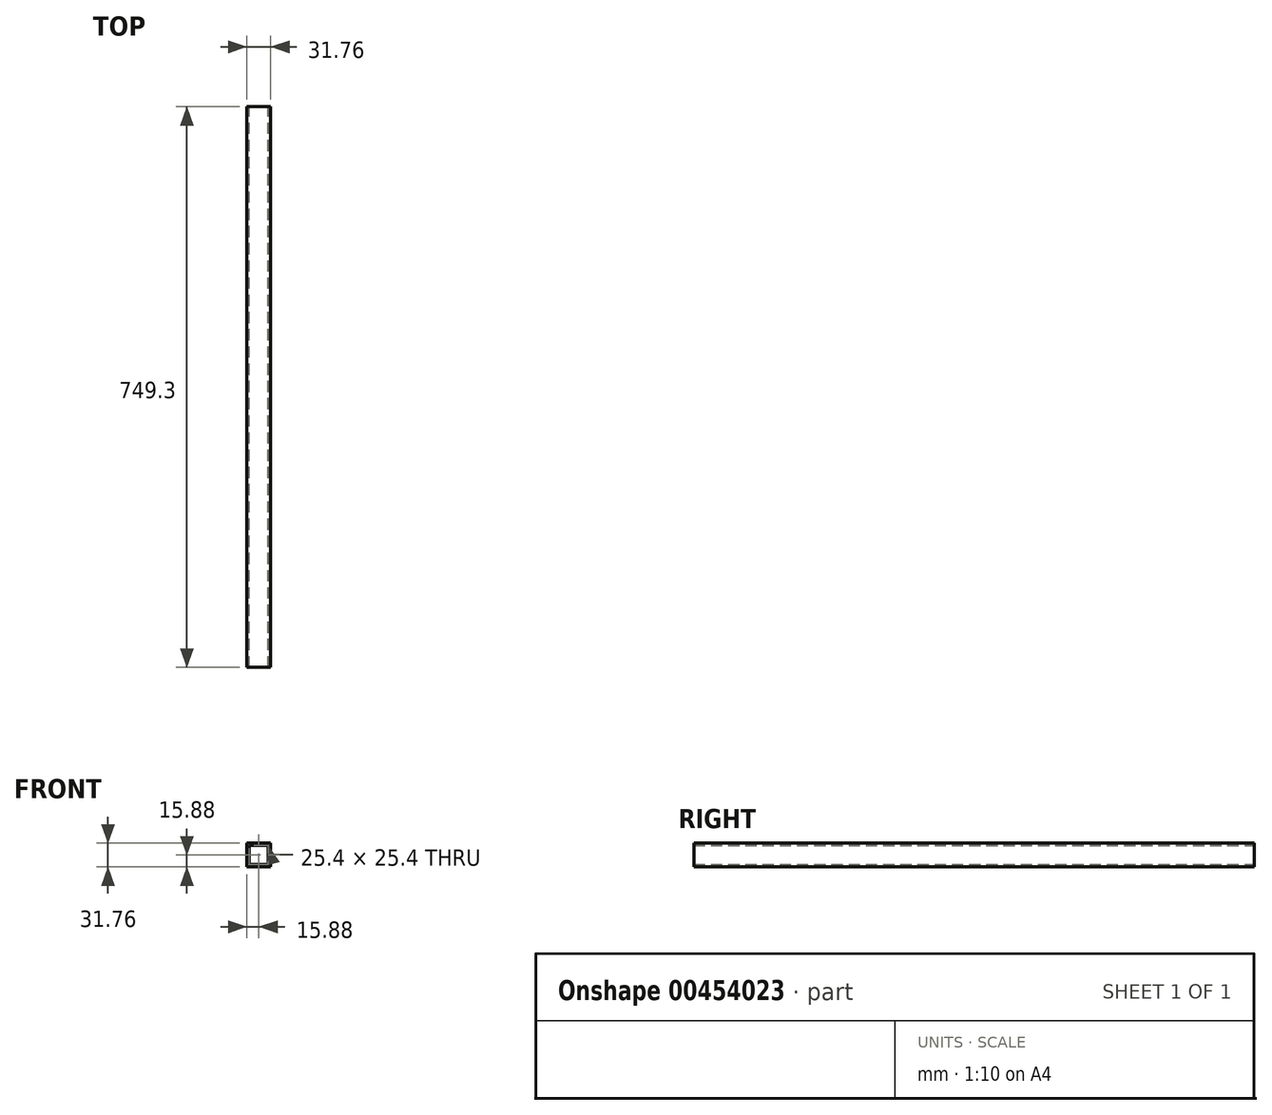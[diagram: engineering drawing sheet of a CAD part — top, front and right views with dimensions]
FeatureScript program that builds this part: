
annotation { "Feature Type Name" : "Feature", "Feature Type Description" : "" }
export const myFeature = defineFeature(function(context is Context, id is Id, definition is map)
    precondition{}
    {
        {
            var Q0;
            Q0=qCreatedBy(makeId("Front.planeOp"),FACE);
            var sketch = newSketch(context, id + "F0", { "sketchPlane" : qUnion([Q0])});
            skLineSegment(sketch, "E0.bottom", {"start": v(-15.87, 15.88) * mm, "end": v(15.88, 15.88) * mm});
            skLineSegment(sketch, "E0.top", {"start": v(-15.88, -15.88) * mm, "end": v(15.88, -15.88) * mm});
            skLineSegment(sketch, "E0.left", {"start": v(-15.87, 15.88) * mm, "end": v(-15.88, -15.88) * mm});
            skLineSegment(sketch, "E0.right", {"start": v(15.88, 15.88) * mm, "end": v(15.88, -15.88) * mm});
            skPoint(sketch, "E0.middle", {"position": v(0, 0) * mm});
            skLineSegment(sketch, "E1.bottom", {"start": v(-12.7, 12.7) * mm, "end": v(12.7, 12.7) * mm});
            skLineSegment(sketch, "E1.top", {"start": v(-12.7, -12.7) * mm, "end": v(12.7, -12.7) * mm});
            skLineSegment(sketch, "E1.left", {"start": v(-12.7, 12.7) * mm, "end": v(-12.7, -12.7) * mm});
            skLineSegment(sketch, "E1.right", {"start": v(12.7, 12.7) * mm, "end": v(12.7, -12.7) * mm});
            skSolve(sketch);
        }
        {
            var Q0;
            Q0=makeQuery(id+"F0.imprint","IMPRINT",FACE,{"disambiguationData":[TD([[makeQuery(id+"F0.imprint","IMPRINT",EDGE,{"derivedFrom":sQuery(id+"F0.wireOp",EDGE,"E0.bottom")}),-1.0]])]});
            extrude(context, id + "F1", {"entities" : qUnion([Q0]), "endBound" : BoundingType.SYMMETRIC, "depth" : 749.3 * mm});
        }
    });
